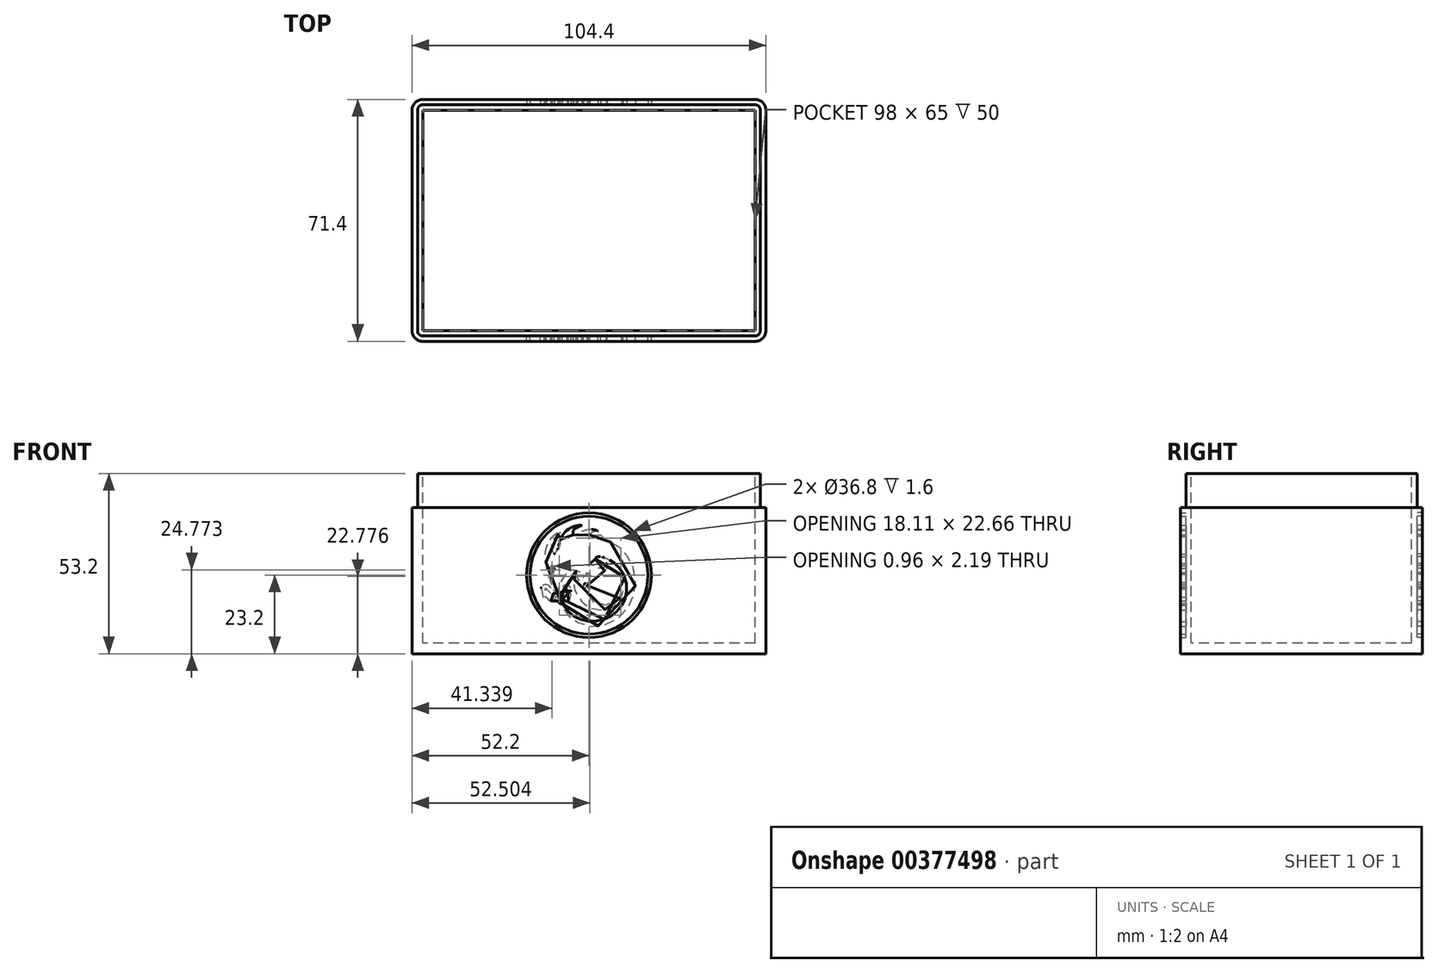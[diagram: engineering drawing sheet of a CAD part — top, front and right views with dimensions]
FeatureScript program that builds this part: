
annotation { "Feature Type Name" : "Feature", "Feature Type Description" : "" }
export const myFeature = defineFeature(function(context is Context, id is Id, definition is map)
    precondition{}
    {
        {
            assignVariable(context, id + "F0", {"name" : "InnerWidth", "anyValue" : 65 * mm});
        }
        {
            assignVariable(context, id + "F1", {"name" : "InnerDepth", "anyValue" : 50 * mm});
        }
        {
            assignVariable(context, id + "F2", {"name" : "WallThickness", "anyValue" : 3.2 * mm});
        }
        {
            assignVariable(context, id + "F3", {"name" : "LidDepth", "anyValue" : 10 * mm});
        }
        {
            var Q0;
            Q0=qCreatedBy(makeId("Top.planeOp"),FACE);
            var sketch = newSketch(context, id + "F4", { "sketchPlane" : qUnion([Q0])});
            skLineSegment(sketch, "E0.bottom", {"start": v(49, 32.5) * mm, "end": v(-49, 32.5) * mm});
            skLineSegment(sketch, "E0.top", {"start": v(49, -32.5) * mm, "end": v(-49, -32.5) * mm});
            skLineSegment(sketch, "E0.left", {"start": v(49, 32.5) * mm, "end": v(49, -32.5) * mm});
            skLineSegment(sketch, "E0.right", {"start": v(-49, 32.5) * mm, "end": v(-49, -32.5) * mm});
            skPoint(sketch, "E0.middle", {"position": v(0, 0) * mm});
            skSolve(sketch);
        }
        {
            var Q0;
            Q0=qCreatedBy(makeId("Top.planeOp"),FACE);
            var sketch = newSketch(context, id + "F5", { "sketchPlane" : qUnion([Q0])});
            skLineSegment(sketch, "E1.bottom", {"start": v(52.2, 35.7) * mm, "end": v(-52.2, 35.7) * mm});
            skLineSegment(sketch, "E1.top", {"start": v(52.2, -35.7) * mm, "end": v(-52.2, -35.7) * mm});
            skLineSegment(sketch, "E1.left", {"start": v(52.2, 35.7) * mm, "end": v(52.2, -35.7) * mm});
            skLineSegment(sketch, "E1.right", {"start": v(-52.2, 35.7) * mm, "end": v(-52.2, -35.7) * mm});
            skPoint(sketch, "E1.middle", {"position": v(0, 0) * mm});
            skSolve(sketch);
        }
        {
            var Q0;
            Q0=qCreatedBy(makeId("Top.planeOp"),FACE);
            var sketch = newSketch(context, id + "F6", { "sketchPlane" : qUnion([Q0])});
            skLineSegment(sketch, "E2.bottom", {"start": v(50.6, 34.1) * mm, "end": v(-50.6, 34.1) * mm});
            skLineSegment(sketch, "E2.top", {"start": v(50.6, -34.1) * mm, "end": v(-50.6, -34.1) * mm});
            skLineSegment(sketch, "E2.left", {"start": v(50.6, 34.1) * mm, "end": v(50.6, -34.1) * mm});
            skLineSegment(sketch, "E2.right", {"start": v(-50.6, 34.1) * mm, "end": v(-50.6, -34.1) * mm});
            skPoint(sketch, "E2.middle", {"position": v(0, 0) * mm});
            skLineSegment(sketch, "E3.bottom", {"start": v(52.2, 35.7) * mm, "end": v(-52.2, 35.7) * mm});
            skLineSegment(sketch, "E3.top", {"start": v(52.2, -35.7) * mm, "end": v(-52.2, -35.7) * mm});
            skLineSegment(sketch, "E3.left", {"start": v(52.2, 35.7) * mm, "end": v(52.2, -35.7) * mm});
            skLineSegment(sketch, "E3.right", {"start": v(-52.2, 35.7) * mm, "end": v(-52.2, -35.7) * mm});
            skSolve(sketch);
        }
        {
            var Q0;
            Q0=qSketchRegion(id+"F5",true);
            extrude(context, id + "F7", {"entities" : qUnion([Q0]), "oppositeDirection" : true, "depth" : getVariable(context, 'InnerDepth') + getVariable(context, 'WallThickness')});
        }
        {
            var Q0;
            Q0=makeQuery(id+"F4.imprint","IMPRINT",FACE,{"disambiguationData":[TD([[makeQuery(id+"F4.imprint","IMPRINT",EDGE,{"derivedFrom":sQuery(id+"F4.wireOp",EDGE,"E0.bottom")}),1.0]])]});
            extrude(context, id + "F8", {"entities" : qUnion([Q0]), "operationType" : NewBodyOperationType.REMOVE, "oppositeDirection" : true, "depth" : getVariable(context, 'InnerDepth')});
        }
        {
            var Q0;
            Q0=makeQuery(id+"F7.opExtrude","SWEPT_EDGE",EDGE,{"disambiguationData":[OSD([sQuery(id+"F5.wireOp",EDGE,"E1.bottom"),sQuery(id+"F5.wireOp",EDGE,"E1.right")])]});
            var Q1;
            Q1=makeQuery(id+"F7.opExtrude","SWEPT_EDGE",EDGE,{"disambiguationData":[OSD([sQuery(id+"F5.wireOp",EDGE,"E1.bottom"),sQuery(id+"F5.wireOp",EDGE,"E1.left")])]});
            var Q2;
            Q2=makeQuery(id+"F7.opExtrude","SWEPT_EDGE",EDGE,{"disambiguationData":[OSD([sQuery(id+"F5.wireOp",EDGE,"E1.top"),sQuery(id+"F5.wireOp",EDGE,"E1.left")])]});
            var Q3;
            Q3=makeQuery(id+"F7.opExtrude","SWEPT_EDGE",EDGE,{"disambiguationData":[OSD([sQuery(id+"F5.wireOp",EDGE,"E1.top"),sQuery(id+"F5.wireOp",EDGE,"E1.right")])]});
            fillet(context, id + "F9", {"entities" : qUnion([Q0, Q1, Q2, Q3]), "radius" : getVariable(context, 'WallThickness'), "tangentPropagation" : true, "allowEdgeOverflow" : false});
        }
        {
            var Q0;
            Q0=qCreatedBy(makeId("Front.planeOp"),FACE);
            var sketch = newSketch(context, id + "F10", { "sketchPlane" : qUnion([Q0])});
            skCircle(sketch, "E4", {"center": v(0, -30) * mm, "radius": 18.4 * mm});
            skCircle(sketch, "E5", {"center": v(0, -30) * mm, "radius": 17.4 * mm});
            skSolve(sketch);
        }
        {
            var Q0;
            Q0=qCreatedBy(makeId("Front.planeOp"),FACE);
            var sketch = newSketch(context, id + "F11", { "sketchPlane" : qUnion([Q0])});
            skPoint(sketch, "E6.middle", {"position": v(0, -30) * mm});
            skFitSpline(sketch, "E7", {"points": [v(-8.72, -36.49) * mm, v(-9, -35.5) * mm, v(-9.04, -33.98) * mm, v(-8.81, -32.85) * mm, v(-8.44, -31.93) * mm, v(-7.78, -31.08) * mm, v(-7.63, -30.82) * mm, v(-7.14, -30.49) * mm, v(-6.49, -29.8) * mm, v(-6.04, -29.11) * mm, v(-5.77, -28.42) * mm, v(-5.61, -27.95) * mm, v(-5.35, -27.9) * mm, v(-5.1, -27.9) * mm, v(-4.95, -27.95) * mm, v(-4.85, -28.3) * mm, v(-4.73, -28.4) * mm, v(-4.04, -28.73) * mm, v(-3.42, -28.91) * mm, v(-2.37, -29.13) * mm, v(-1.23, -29.24) * mm, v(-0.27, -29.24) * mm, v(0.25, -29.2) * mm, v(-0.72, -29.68) * mm, v(-1.8, -30.42) * mm, v(-2.82, -31.47) * mm, v(-3.25, -32.1) * mm, v(-3.58, -31.53) * mm, v(-3.77, -30.79) * mm, v(-3.6, -30.15) * mm, v(-3.32, -29.76) * mm, v(-3.86, -30.04) * mm, v(-4.4, -30.92) * mm, v(-4.58, -32.08) * mm, v(-4.55, -32.9) * mm, v(-4.37, -33.72) * mm, v(-4, -34.92) * mm, v(-3.26, -36.33) * mm, v(-2.4, -37.51) * mm, v(-1.43, -38.47) * mm, v(-0.63, -39.09) * mm, v(0.15, -39.57) * mm, v(1.05, -39.97) * mm, v(2.35, -40.27) * mm, v(3.61, -40.32) * mm, v(4.73, -40.18) * mm, v(5.83, -39.89) * mm, v(6.78, -39.48) * mm, v(7.49, -39.13) * mm, v(8.19, -38.6) * mm, v(8.86, -37.9) * mm, v(9.45, -37.07) * mm, v(9.83, -36.27) * mm, v(10.05, -35.2) * mm, v(9.97, -34.35) * mm, v(9.74, -33.6) * mm, v(9.62, -33.46) * mm, v(9.69, -33.71) * mm, v(9.74, -34.74) * mm, v(9.56, -35.8) * mm, v(9.1, -36.72) * mm, v(8, -37.8) * mm, v(6.7, -38.45) * mm, v(5.18, -38.8) * mm, v(3.92, -38.8) * mm, v(2.72, -38.58) * mm, v(1.61, -38.08) * mm, v(0.77, -37.4) * mm, v(0.16, -36.56) * mm, v(-0.23, -35.68) * mm, v(-0.44, -34.51) * mm, v(-0.4, -33.4) * mm, v(-0.32, -33.03) * mm, v(-0.32, -32.84) * mm, v(-0.48, -33) * mm, v(-0.61, -33.22) * mm, v(-0.8, -33.66) * mm, v(-1, -33.91) * mm, v(-1.25, -34.01) * mm, v(-1.38, -33.98) * mm, v(-1.53, -33.73) * mm, v(-1.58, -33.48) * mm, v(-1.6, -33.15) * mm, v(-1.49, -32.86) * mm, v(-1.27, -32.52) * mm, v(-1.18, -32.45) * mm, v(-0.5, -32.25) * mm, v(0.3, -31.9) * mm, v(1.54, -31.25) * mm, v(2, -30.96) * mm, v(2.57, -30.55) * mm, v(3.06, -30.08) * mm, v(3.52, -29.68) * mm, v(4.17, -29.27) * mm, v(4.5, -28.85) * mm, v(4.82, -28.52) * mm, v(5.18, -27.97) * mm, v(5.33, -27.22) * mm, v(5.26, -26.76) * mm, v(5.14, -26.51) * mm, v(5.15, -26.73) * mm, v(5.07, -27.1) * mm, v(4.89, -27.5) * mm, v(4.63, -27.72) * mm, v(4.26, -27.86) * mm, v(3.58, -27.94) * mm, v(2.63, -27.81) * mm, v(1.52, -27.34) * mm, v(0.71, -26.8) * mm, v(0.3, -26.56) * mm, v(0.17, -26.5) * mm, v(0.3, -26.42) * mm, v(1.03, -25.99) * mm, v(1.63, -25.4) * mm, v(2.16, -24.8) * mm, v(2.27, -24.58) * mm, v(2.33, -24.5) * mm, v(2.47, -24.5) * mm, v(3.1, -24.5) * mm, v(3.83, -24.63) * mm, v(4.67, -24.86) * mm, v(5.46, -25.16) * mm, v(6.02, -25.42) * mm, v(6.6, -25.77) * mm, v(7.16, -26.14) * mm, v(7.95, -26.8) * mm, v(8.6, -27.48) * mm, v(9.24, -28.25) * mm, v(9.66, -28.86) * mm, v(10.01, -29.46) * mm, v(10.33, -30.14) * mm, v(10.67, -31.04) * mm, v(10.89, -31.8) * mm, v(11, -32.54) * mm, v(11.14, -33.64) * mm, v(11.06, -34.88) * mm, v(10.78, -36.42) * mm, v(10.4, -37.43) * mm, v(9.81, -38.65) * mm, v(9.06, -39.76) * mm, v(7.86, -41.03) * mm, v(6.74, -41.9) * mm, v(5.8, -42.44) * mm, v(4.56, -43.01) * mm, v(3.22, -43.4) * mm, v(1.46, -43.62) * mm, v(0.43, -43.65) * mm, v(-0.69, -43.53) * mm, v(-2.13, -43.2) * mm, v(-3.12, -42.83) * mm, v(-4.26, -42.22) * mm, v(-5.35, -41.5) * mm, v(-6.3, -40.65) * mm, v(-7.13, -39.55) * mm, v(-7.6, -38.4) * mm, v(-7.85, -37.28) * mm, v(-7.92, -36.02) * mm, v(-7.81, -34.93) * mm, v(-7.6, -34.3) * mm, v(-7.26, -33.82) * mm, v(-7.1, -33.71) * mm, v(-6.97, -33.82) * mm, v(-6.63, -34.23) * mm, v(-6.32, -35.02) * mm, v(-6.14, -36.05) * mm, v(-6.14, -37.28) * mm, v(-6.32, -38.09) * mm, v(-6.42, -38.33) * mm, v(-6.2, -38.13) * mm, v(-5.9, -37.57) * mm, v(-5.52, -36.44) * mm, v(-5.3, -35.2) * mm, v(-5.38, -34.14) * mm, v(-5.7, -33.34) * mm, v(-5.87, -33.15) * mm, v(-6.26, -32.89) * mm, v(-6.94, -32.87) * mm, v(-7.18, -32.92) * mm, v(-7.5, -33.2) * mm, v(-7.97, -33.84) * mm, v(-8.36, -34.77) * mm, v(-8.49, -35.96) * mm, v(-8.48, -36.47) * mm, v(-8.47, -37.36) * mm, v(-8.46, -37.56) * mm, v(-8.6, -37.36) * mm, v(-9.08, -36.9) * mm, v(-9.73, -36.44) * mm, v(-9.93, -36.3) * mm, v(-10.3, -35.9) * mm, v(-10.57, -35.4) * mm, v(-10.76, -34.9) * mm, v(-10.93, -34.29) * mm, v(-11.21, -33.68) * mm, v(-11.64, -33.2) * mm, v(-12.45, -32.81) * mm, v(-13.15, -32.81) * mm, v(-13.72, -33.12) * mm, v(-14.13, -33.72) * mm, v(-14.33, -34.56) * mm, v(-14.17, -35.37) * mm, v(-13.9, -36.1) * mm, v(-13.52, -36.64) * mm, v(-13, -37.08) * mm, v(-12.42, -37.39) * mm, v(-11.72, -37.6) * mm, v(-11.34, -37.67) * mm, v(-11.15, -37.61) * mm, v(-11.34, -37.56) * mm, v(-11.9, -37.3) * mm, v(-12.55, -36.83) * mm, v(-13.04, -36.11) * mm, v(-13.2, -35.23) * mm, v(-13.16, -34.42) * mm, v(-13, -34.1) * mm, v(-12.75, -33.76) * mm, v(-12.52, -33.67) * mm, v(-12.3, -33.73) * mm, v(-11.99, -33.87) * mm, v(-11.63, -34.47) * mm, v(-11.4, -35.2) * mm, v(-11.24, -35.63) * mm, v(-10.98, -36.1) * mm, v(-10.7, -36.49) * mm, v(-10.46, -36.73) * mm, v(-9.78, -37.24) * mm, v(-9.12, -37.78) * mm, v(-8.63, -38.36) * mm, v(-8.24, -38.9) * mm, v(-7.78, -39.7) * mm, v(-7.1, -40.64) * mm, v(-6.16, -41.76) * mm, v(-5.71, -42.19) * mm, v(-5.14, -42.7) * mm, v(-4.13, -43.45) * mm, v(-3.1, -44.1) * mm, v(-1.87, -44.6) * mm, v(-0.23, -44.98) * mm, v(1.66, -45.1) * mm, v(3, -45) * mm, v(4.5, -44.7) * mm, v(5.96, -44.2) * mm, v(7.6, -43.36) * mm, v(9.12, -42.27) * mm, v(10.28, -41.18) * mm, v(11.2, -40.03) * mm, v(12.09, -38.69) * mm, v(12.8, -37.11) * mm, v(13.29, -35.7) * mm, v(13.63, -33.91) * mm, v(13.76, -32.53) * mm, v(13.74, -31.08) * mm, v(13.5, -29.44) * mm, v(13.2, -28.18) * mm, v(12.63, -26.63) * mm, v(12.2, -25.78) * mm, v(11.62, -24.78) * mm, v(10.87, -23.73) * mm, v(10, -22.74) * mm, v(8.96, -21.8) * mm, v(7.77, -20.95) * mm, v(6.87, -20.45) * mm, v(6.01, -20.02) * mm, v(4.57, -19.5) * mm, v(3.78, -19.33) * mm, v(3.63, -19.27) * mm, v(3.51, -19.1) * mm, v(3.52, -18.9) * mm, v(3.7, -18.77) * mm, v(4.06, -18.6) * mm, v(4.34, -18.53) * mm, v(4.84, -18.5) * mm, v(5.05, -18.5) * mm, v(4.88, -18.32) * mm, v(4.35, -18.16) * mm, v(3.57, -18.06) * mm, v(2.6, -18.13) * mm, v(1.54, -18.45) * mm, v(1.18, -18.58) * mm, v(0.95, -18.55) * mm, v(0.62, -18.5) * mm, v(0.4, -18.4) * mm, v(0.3, -18.32) * mm, v(0.24, -18.18) * mm, v(0.2, -18.07) * mm, v(0.48, -17.74) * mm, v(0.9, -17.35) * mm, v(1.57, -17.04) * mm, v(2.22, -16.96) * mm, v(2.5, -16.94) * mm, v(2.66, -16.93) * mm, v(2.45, -16.82) * mm, v(1.94, -16.66) * mm, v(1.15, -16.56) * mm, v(-0.2, -16.57) * mm, v(-1.26, -16.82) * mm, v(-2.07, -17.07) * mm, v(-2.45, -17.35) * mm, v(-3.13, -17.77) * mm, v(-3.53, -18) * mm, v(-3.84, -18.14) * mm, v(-4.2, -18.18) * mm, v(-4.44, -18.07) * mm, v(-4.59, -17.91) * mm, v(-4.65, -17.7) * mm, v(-4.7, -17.26) * mm, v(-4.64, -16.91) * mm, v(-4.4, -16.5) * mm, v(-3.98, -16.13) * mm, v(-3.27, -15.76) * mm, v(-2.36, -15.4) * mm, v(-2.15, -15.32) * mm, v(-2.39, -15.25) * mm, v(-3.28, -15.33) * mm, v(-4.25, -15.58) * mm, v(-5.37, -16.04) * mm, v(-6.4, -16.68) * mm, v(-7.31, -17.64) * mm, v(-7.86, -18.42) * mm, v(-8.38, -19.38) * mm, v(-8.6, -19.85) * mm, v(-8.67, -19.99) * mm, v(-8.74, -20.4) * mm, v(-8.9, -21.3) * mm, v(-9.08, -22) * mm, v(-9.58, -22.84) * mm, v(-9.98, -23.35) * mm, v(-10.14, -23.54) * mm, v(-10.23, -23.77) * mm, v(-10.32, -23.63) * mm, v(-10.43, -23.36) * mm, v(-10.71, -22.77) * mm, v(-10.9, -22.21) * mm, v(-10.94, -21.34) * mm, v(-10.86, -20.63) * mm, v(-10.6, -19.86) * mm, v(-10.1, -18.97) * mm, v(-9.34, -18.1) * mm, v(-8.59, -17.46) * mm, v(-8.26, -17.2) * mm, v(-7.92, -16.88) * mm, v(-7.92, -16.8) * mm, v(-8.08, -16.89) * mm, v(-8.7, -17.18) * mm, v(-9.76, -17.8) * mm, v(-11.35, -19.29) * mm, v(-12.26, -20.8) * mm, v(-12.6, -21.73) * mm, v(-12.94, -22.8) * mm, v(-13.01, -23.63) * mm, v(-13.05, -24.6) * mm, v(-13, -25.47) * mm, v(-12.97, -25.57) * mm, v(-12.86, -25.74) * mm, v(-12.62, -26.42) * mm, v(-12.52, -27.24) * mm, v(-12.55, -28.1) * mm, v(-12.55, -28.87) * mm, v(-12.46, -29.13) * mm, v(-12.24, -29.57) * mm, v(-11.88, -30.33) * mm, v(-11.53, -31.16) * mm, v(-11.3, -31.9) * mm, v(-11.04, -32.88) * mm, v(-10.77, -33.62) * mm, v(-10.46, -34.26) * mm, v(-10.26, -34.7) * mm, v(-9.94, -35.22) * mm, v(-9.5, -35.78) * mm, v(-9.1, -36.22) * mm, v(-8.89, -36.42) * mm, v(-8.72, -36.49) * mm]});
            skFitSpline(sketch, "E8", {"points": [v(-11.12, -29.52) * mm, v(-11.17, -29.39) * mm, v(-11.24, -29.24) * mm, v(-11.3, -29.12) * mm, v(-11.34, -28.86) * mm, v(-11.28, -28.6) * mm, v(-11.2, -28.19) * mm, v(-11.12, -27.79) * mm, v(-11.13, -27.64) * mm, v(-11, -27.4) * mm, v(-10.9, -27.22) * mm, v(-10.87, -27.15) * mm, v(-10.84, -27.22) * mm, v(-10.75, -27.34) * mm, v(-10.64, -27.5) * mm, v(-10.52, -27.63) * mm, v(-10.42, -27.8) * mm, v(-10.33, -28) * mm, v(-10.32, -28.22) * mm, v(-10.37, -28.46) * mm, v(-10.48, -28.73) * mm, v(-10.61, -28.9) * mm, v(-10.77, -29.08) * mm, v(-10.89, -29.2) * mm, v(-10.98, -29.34) * mm, v(-11.06, -29.45) * mm, v(-11.12, -29.52) * mm]});
            skSolve(sketch);
        }
        {
            var Q0;
            Q0 = qSketchRegion(id + "F11", true);
            var Q1;
            Q1 = qSketchRegion(id + "F10", true);
            extrude(context, id + "F12", {"entities" : qUnion([Q0, Q1]), "operationType" : NewBodyOperationType.REMOVE, "depth" : getVariable(context, 'InnerWidth') / 2 + getVariable(context, 'WallThickness'), "hasSecondDirection" : true, "secondDirectionOppositeDirection" : false, "secondDirectionDepth" : getVariable(context, 'InnerWidth') / 2 + getVariable(context, 'WallThickness') / 2});
        }
        {
            var Q0;
            Q0 = qSketchRegion(id + "F11", true);
            var Q1;
            Q1 = qSketchRegion(id + "F10", true);
            extrude(context, id + "F13", {"entities" : qUnion([Q0, Q1]), "operationType" : NewBodyOperationType.REMOVE, "oppositeDirection" : true, "depth" : getVariable(context, 'InnerWidth') / 2 + getVariable(context, 'WallThickness'), "hasSecondDirection" : true, "secondDirectionOppositeDirection" : true, "secondDirectionDepth" : getVariable(context, 'InnerWidth') / 2 + getVariable(context, 'WallThickness') / 2});
        }
        {
            var Q0;
            Q0 = qSketchRegion(id + "F6", true);
            extrude(context, id + "F14", {"entities" : qUnion([Q0]), "operationType" : NewBodyOperationType.REMOVE, "oppositeDirection" : true, "depth" : getVariable(context, 'LidDepth')});
        }
        {
            var Q0;
            Q0=makeQuery(id+"F14.boolean.opBoolean","COPY",EDGE,{"derivedFrom":makeQuery(id+"F14.opExtrude","SWEPT_EDGE",EDGE,{"disambiguationData":[OSD([sQuery(id+"F6.wireOp",EDGE,"E2.top"),sQuery(id+"F6.wireOp",EDGE,"E2.left")])]})});
            var Q1;
            Q1=makeQuery(id+"F14.boolean.opBoolean","COPY",EDGE,{"derivedFrom":makeQuery(id+"F14.opExtrude","SWEPT_EDGE",EDGE,{"disambiguationData":[OSD([sQuery(id+"F6.wireOp",EDGE,"E2.top"),sQuery(id+"F6.wireOp",EDGE,"E2.right")])]})});
            var Q2;
            Q2=makeQuery(id+"F14.boolean.opBoolean","COPY",EDGE,{"derivedFrom":makeQuery(id+"F14.opExtrude","SWEPT_EDGE",EDGE,{"disambiguationData":[OSD([sQuery(id+"F6.wireOp",EDGE,"E2.bottom"),sQuery(id+"F6.wireOp",EDGE,"E2.left")])]})});
            var Q3;
            Q3=makeQuery(id+"F14.boolean.opBoolean","COPY",EDGE,{"derivedFrom":makeQuery(id+"F14.opExtrude","SWEPT_EDGE",EDGE,{"disambiguationData":[OSD([sQuery(id+"F6.wireOp",EDGE,"E2.bottom"),sQuery(id+"F6.wireOp",EDGE,"E2.right")])]})});
            fillet(context, id + "F15", {"entities" : qUnion([Q0, Q1, Q2, Q3]), "radius" : getVariable(context, 'WallThickness') / 2, "tangentPropagation" : true, "allowEdgeOverflow" : false});
        }
    });
